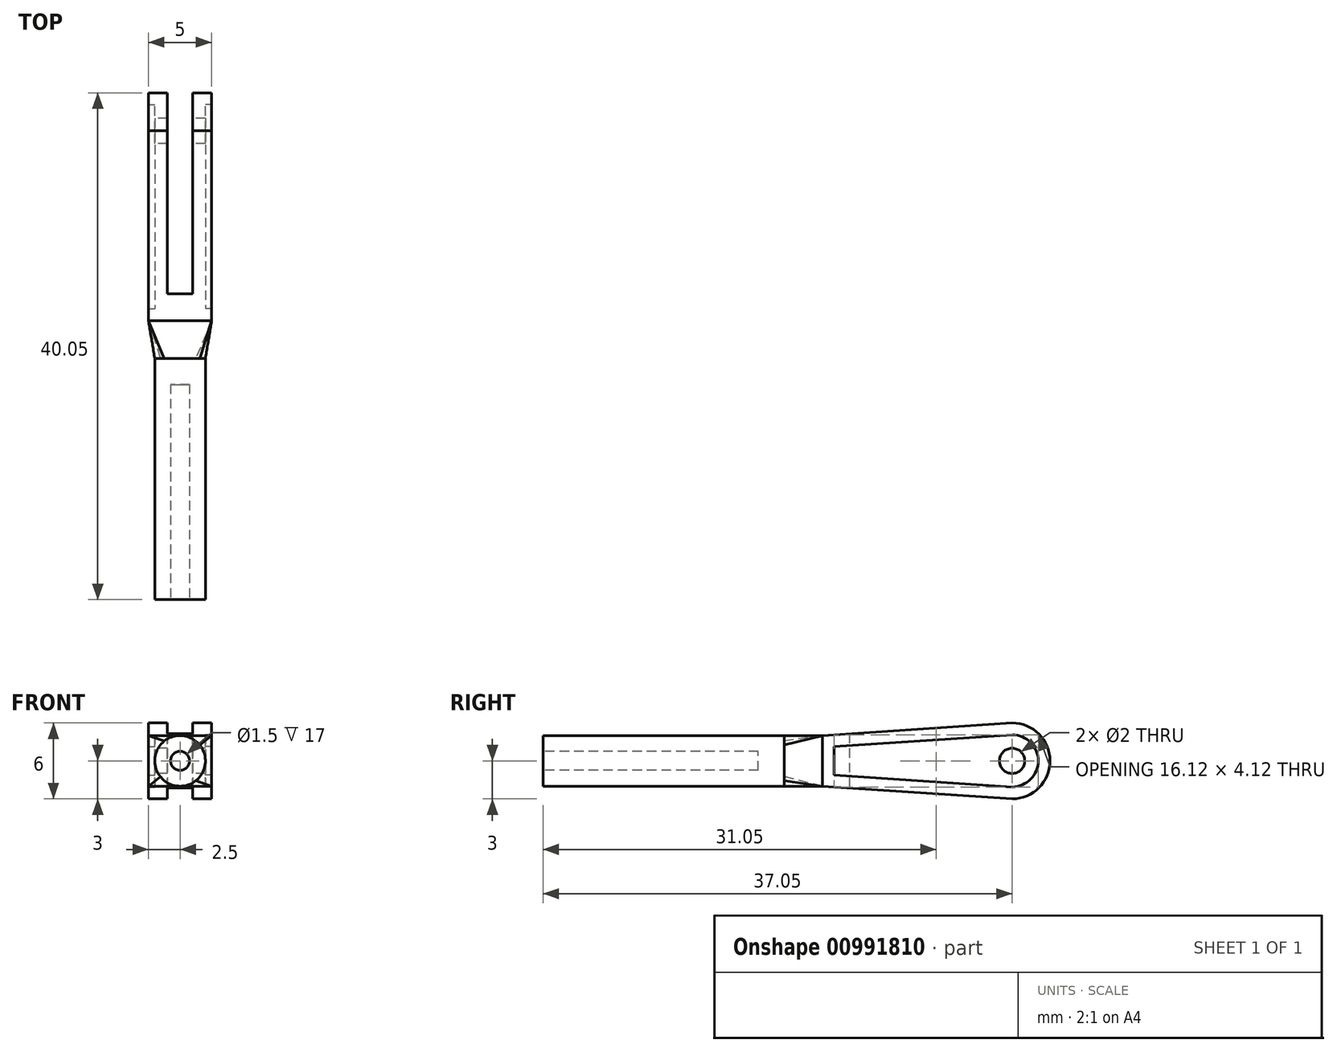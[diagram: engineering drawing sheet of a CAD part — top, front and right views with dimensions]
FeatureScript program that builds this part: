
annotation { "Feature Type Name" : "Feature", "Feature Type Description" : "" }
export const myFeature = defineFeature(function(context is Context, id is Id, definition is map)
    precondition{}
    {
        {
            var Q0;
            Q0=qCreatedBy(makeId("Front.planeOp"),FACE);
            var sketch = newSketch(context, id + "F0", { "sketchPlane" : qUnion([Q0])});
            skCircle(sketch, "E0", {"center": v(0, 0) * mm, "radius": 2 * mm});
            skCircle(sketch, "E1", {"center": v(0, 0) * mm, "radius": 0.75 * mm});
            skSolve(sketch);
        }
        {
            var Q0;
            Q0=makeQuery(id+"F0.imprint","IMPRINT",FACE,{"disambiguationData":[TD([[makeQuery(id+"F0.imprint","IMPRINT",EDGE,{"derivedFrom":sQuery(id+"F0.wireOp",EDGE,"E0")}),1.0]])]});
            var Q1;
            Q1=makeQuery(id+"F0.imprint","IMPRINT",FACE,{"disambiguationData":[TD([[makeQuery(id+"F0.imprint","IMPRINT",EDGE,{"derivedFrom":sQuery(id+"F0.wireOp",EDGE,"E1")}),1.0]])]});
            extrude(context, id + "F1", {"entities" : qUnion([Q0, Q1]), "depth" : 19.05 * mm, "offsetDistance" : 25.4 * mm});
        }
        {
            var Q0;
            Q0=qCreatedBy(makeId("Right.planeOp"),FACE);
            var sketch = newSketch(context, id + "F2", { "sketchPlane" : qUnion([Q0])});
            skLineSegment(sketch, "E2.0", {"start": v(3, -2) * mm, "end": v(3, 2) * mm});
            skCircle(sketch, "E3", {"center": v(18, 0) * mm, "radius": 3 * mm});
            skLineSegment(sketch, "E4", {"start": v(18, -3) * mm, "end": v(18, 3) * mm, "construction": true});
            skLineSegment(sketch, "E5", {"start": v(18, 3) * mm, "end": v(3, 2) * mm});
            skLineSegment(sketch, "E6", {"start": v(18, -3) * mm, "end": v(3, -2) * mm});
            skCircle(sketch, "E7", {"center": v(18, 0) * mm, "radius": 1 * mm});
            skSolve(sketch);
        }
        {
            var Q0;
            Q0=makeQuery(id+"F2.imprint","IMPRINT",FACE,{"disambiguationData":[TD([[makeQuery(id+"F2.imprint","IMPRINT",EDGE,{"derivedFrom":sQuery(id+"F2.wireOp",EDGE,"waPN0C9D-aEQh-yq3H-stLx-nCHPpKASFijS")}),1.0]])]});
            var Q1;
            {var subQ0=sQuery(id+"F2.wireOp",EDGE,"E2.0");Q1=makeQuery(id+"F2.imprint","IMPRINT",FACE,{"disambiguationData":[TD([[makeQuery(id+"F2.imprint","IMPRINT",EDGE,{"derivedFrom":subQ0}),-1.0]])]});}
            var Q2;
            Q2=makeQuery(id+"F2.imprint","IMPRINT",FACE,{"disambiguationData":[TD([[makeQuery(id+"F2.imprint","IMPRINT",EDGE,{"derivedFrom":sQuery(id+"F2.wireOp",EDGE,"E7")}),-1.0]])]});
            extrude(context, id + "F3", {"entities" : qUnion([Q0, Q1, Q2]), "endBound" : BoundingType.SYMMETRIC, "depth" : 4 * mm, "offsetDistance" : 25.4 * mm});
        }
        {
            var Q0;
            Q0=qCreatedBy(makeId("Top.planeOp"),FACE);
            var sketch = newSketch(context, id + "F4", { "sketchPlane" : qUnion([Q0])});
            skLineSegment(sketch, "E8.bottom", {"start": v(1, 26.49) * mm, "end": v(-1, 26.49) * mm});
            skLineSegment(sketch, "E8.top", {"start": v(1, 5.13) * mm, "end": v(-1, 5.13) * mm});
            skLineSegment(sketch, "E8.left", {"start": v(1, 26.49) * mm, "end": v(1, 5.13) * mm});
            skLineSegment(sketch, "E8.right", {"start": v(-1, 26.49) * mm, "end": v(-1, 5.13) * mm});
            skPoint(sketch, "E8.middle", {"position": v(0, 15.8) * mm});
            skSolve(sketch);
        }
        {
            var Q0;
            Q0=makeQuery(id+"F4.imprint","IMPRINT",FACE,{"disambiguationData":[TD([[makeQuery(id+"F4.imprint","IMPRINT",EDGE,{"derivedFrom":sQuery(id+"F4.wireOp",EDGE,"E8.bottom")}),1.0]])]});
            extrude(context, id + "F5", {"entities" : qUnion([Q0]), "endBound" : BoundingType.SYMMETRIC, "depth" : 25 * mm, "offsetDistance" : 25 * mm});
        }
        {
            var Q0;
            Q0=makeQuery(id+"F5.opExtrude","SWEPT_BODY",BODY,{"disambiguationData":[OSD([sQuery(id+"F4.wireOp",EDGE,"E8.bottom"),sQuery(id+"F4.wireOp",EDGE,"E8.top"),sQuery(id+"F4.wireOp",EDGE,"E8.left"),sQuery(id+"F4.wireOp",EDGE,"E8.right")])]});
            var Q1;
            Q1=makeQuery(id+"F3.opExtrude","SWEPT_BODY",BODY,{"disambiguationData":[OSD([sQuery(id+"F2.wireOp",EDGE,"E2.0"),sQuery(id+"F2.wireOp",EDGE,"E3"),sQuery(id+"F2.wireOp",EDGE,"E5"),sQuery(id+"F2.wireOp",EDGE,"E6"),sQuery(id+"F2.wireOp",EDGE,"E7")])]});
            booleanBodies(context, id + "F6", {"operationType" : BooleanOperationType.SUBTRACTION, "tools" : qUnion([Q0]), "targets" : qUnion([Q1])});
        }
        {
            var Q0;
            Q0=makeQuery(id+"F1.opExtrude","CAP_FACE",FACE,{"disambiguationData":[OSD([sQuery(id+"F0.wireOp",EDGE,"E0")])],"isStart":false});
            var sketch = newSketch(context, id + "F7", { "sketchPlane" : qUnion([Q0])});
            skCircle(sketch, "E9", {"center": v(0, 0) * mm, "radius": 0.75 * mm});
            skSolve(sketch);
        }
        {
            var Q0;
            Q0 = qSketchRegion(id + "F7", true);
            extrude(context, id + "F8", {"entities" : qUnion([Q0]), "operationType" : NewBodyOperationType.REMOVE, "oppositeDirection" : true, "depth" : 17 * mm, "offsetDistance" : 25 * mm});
        }
        {
            var Q0;
            Q0=makeQuery(id+"F3.opExtrude","CAP_FACE",FACE,{"disambiguationData":[OSD([sQuery(id+"F2.wireOp",EDGE,"E2.0"),sQuery(id+"F2.wireOp",EDGE,"E3"),sQuery(id+"F2.wireOp",EDGE,"E5"),sQuery(id+"F2.wireOp",EDGE,"E6"),sQuery(id+"F2.wireOp",EDGE,"E7")])],"isStart":true});
            var sketch = newSketch(context, id + "F9", { "sketchPlane" : qUnion([Q0])});
            skLineSegment(sketch, "E10.0", {"start": v(-18.03, -2.06) * mm, "end": v(-3.94, -1.12) * mm});
            skArc(sketch, "E10.1", {"start": v(-18.03, 2.06) * mm, "mid": v(-20.06, 0) * mm, "end": v(-18.03, -2.06) * mm});
            skLineSegment(sketch, "E10.2", {"start": v(-3.94, 1.12) * mm, "end": v(-18.03, 2.06) * mm});
            skLineSegment(sketch, "E10.3", {"start": v(-3.94, -1.12) * mm, "end": v(-3.94, 1.12) * mm});
            skLineSegment(sketch, "E11.0", {"start": v(-18, 3) * mm, "end": v(-3, 2) * mm});
            skArc(sketch, "E11.1", {"start": v(-18, -3) * mm, "mid": v(-21, 0) * mm, "end": v(-18, 3) * mm});
            skLineSegment(sketch, "E11.2", {"start": v(-18, -3) * mm, "end": v(-3, -2) * mm});
            skLineSegment(sketch, "E11.3", {"start": v(-3, -2) * mm, "end": v(-3, 2) * mm});
            skSolve(sketch);
        }
        {
            var Q0;
            Q0 = qSketchRegion(id + "F9", true);
            var Q1;
            Q1=makeQuery(id+"F9.imprint","IMPRINT",FACE,{"disambiguationData":[TD([[makeQuery(id+"F9.imprint","IMPRINT",EDGE,{"derivedFrom":sQuery(id+"F9.wireOp",EDGE,"E10.0")}),-1.0]])]});
            extrude(context, id + "F10", {"entities" : qUnion([Q0, Q1]), "depth" : .5 * mm, "offsetDistance" : 25 * mm});
        }
        {
            var Q0;
            Q0=makeQuery(id+"F10.opExtrude","SWEPT_BODY",BODY,{"disambiguationData":[OSD([sQuery(id+"F9.wireOp",EDGE,"E10.0"),sQuery(id+"F9.wireOp",EDGE,"E10.1"),sQuery(id+"F9.wireOp",EDGE,"E10.2"),sQuery(id+"F9.wireOp",EDGE,"E10.3"),sQuery(id+"F9.wireOp",EDGE,"E11.0"),sQuery(id+"F9.wireOp",EDGE,"E11.1"),sQuery(id+"F9.wireOp",EDGE,"E11.2"),sQuery(id+"F9.wireOp",EDGE,"E11.3")])]});
            var Q1;
            Q1=qCreatedBy(makeId("Right.planeOp"),FACE);
            mirror(context, id + "F11", {"operationType" : NewBodyOperationType.ADD, "entities" : qUnion([Q0]), "mirrorPlane" : qUnion([Q1])});
        }
        {
            var Q0;
            Q0=makeQuery(id+"F3.opExtrude","SWEPT_FACE",FACE,{"disambiguationData":[OSD([sQuery(id+"F2.wireOp",EDGE,"E2.0")])]});
            var sketch = newSketch(context, id + "F12", { "sketchPlane" : qUnion([Q0])});
            skPoint(sketch, "E12.0", {"position": v(2.5, 2) * mm});
            skPoint(sketch, "E12.1", {"position": v(-2.5, -2) * mm});
            skLineSegment(sketch, "E13.bottom", {"start": v(2.5, 2) * mm, "end": v(-2.5, 2) * mm});
            skLineSegment(sketch, "E13.top", {"start": v(2.5, -2) * mm, "end": v(-2.5, -2) * mm});
            skLineSegment(sketch, "E13.left", {"start": v(2.5, 2) * mm, "end": v(2.5, -2) * mm});
            skLineSegment(sketch, "E13.right", {"start": v(-2.5, 2) * mm, "end": v(-2.5, -2) * mm});
            skSolve(sketch);
        }
        {
            var Q0;
            Q0=makeQuery(id+"F1.opExtrude","CAP_FACE",FACE,{"disambiguationData":[OSD([sQuery(id+"F0.wireOp",EDGE,"E0")])],"isStart":true});
            var sketch = newSketch(context, id + "F13", { "sketchPlane" : qUnion([Q0])});
            skArc(sketch, "E14", {"start": v(-1.55, 1.27) * mm, "mid": v(-2, 0) * mm, "end": v(-1.54, -1.28) * mm});
            skArc(sketch, "E15", {"start": v(-1.54, -1.28) * mm, "mid": v(-0.03, -2) * mm, "end": v(1.5, -1.32) * mm});
            skArc(sketch, "E16", {"start": v(1.5, -1.32) * mm, "mid": v(2, -0.08) * mm, "end": v(1.6, 1.19) * mm});
            skArc(sketch, "E17", {"start": v(1.6, 1.19) * mm, "mid": v(0.05, 2) * mm, "end": v(-1.55, 1.27) * mm});
            skSolve(sketch);
        }
        {
            var Q0;
            Q0 = qSketchRegion(id + "F12", true);
            var Q1;
            Q1=makeQuery(id+"F1.opExtrude","CAP_FACE",FACE,{"disambiguationData":[OSD([sQuery(id+"F0.wireOp",EDGE,"E0")])],"isStart":true});
            var Q2;
            Q2=sQuery(id+"F12.wireOp",VERTEX,"E12.1");
            var Q3;
            Q3=sQuery(id+"F13.wireOp",VERTEX,"E15.end");
            var Q4;
            Q4=sQuery(id+"F13.wireOp",VERTEX,"E14.end");
            var Q5;
            Q5=sQuery(id+"F12.wireOp",VERTEX,"E13.top.start");
            loft(context, id + "F14", {"operationType" : NewBodyOperationType.ADD, "sheetProfilesArray" : [{ "sheetProfileEntities" : qUnion([Q0]) }, { "sheetProfileEntities" : qUnion([Q1]) }], "connections" : [{ "connectionEntities" : qUnion([Q2, Q3, Q4, Q5]), "connectionEdgeQueries" : qUnion([]), "connectionEdgeParameters" : [] }]});
        }
    });
